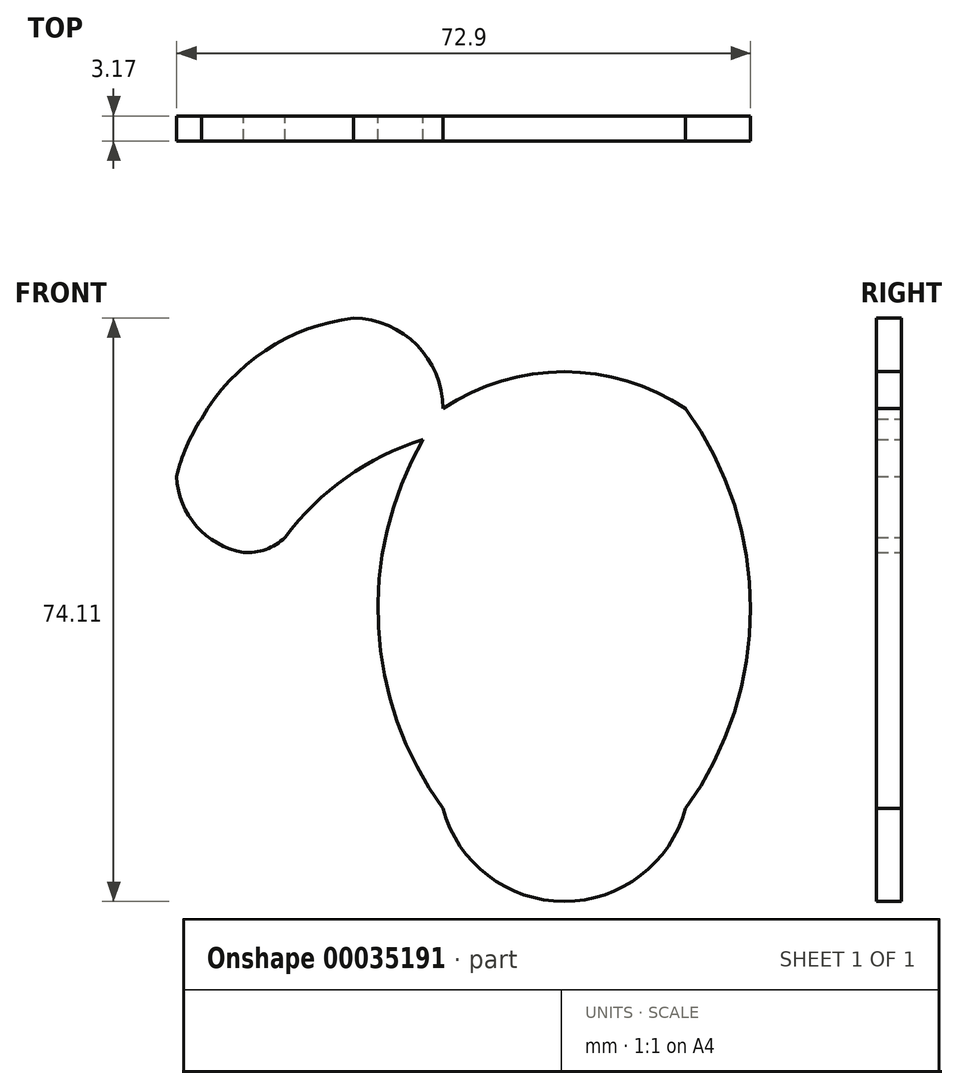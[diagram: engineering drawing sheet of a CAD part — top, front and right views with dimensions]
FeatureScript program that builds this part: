
annotation { "Feature Type Name" : "Feature", "Feature Type Description" : "" }
export const myFeature = defineFeature(function(context is Context, id is Id, definition is map)
    precondition{}
    {
        {
            var Q0;
            Q0=qCreatedBy(makeId("Front.planeOp"),FACE);
            var sketch = newSketch(context, id + "F0", { "sketchPlane" : qUnion([Q0])});
            skLineSegment(sketch, "E0.rect.bottom", {"start": v(15.4, -25.4) * mm, "end": v(-15.4, -25.4) * mm});
            skLineSegment(sketch, "E0.rect.top", {"start": v(15.4, 25.4) * mm, "end": v(-15.4, 25.4) * mm});
            skLineSegment(sketch, "E0.rect.left", {"start": v(15.4, -25.4) * mm, "end": v(15.4, 25.4) * mm});
            skLineSegment(sketch, "E0.rect.right", {"start": v(-15.4, -25.4) * mm, "end": v(-15.4, 25.4) * mm});
            skPoint(sketch, "E0.rect.middle", {"position": v(0, 0) * mm});
            skArc(sketch, "E1", {"start": v(-15.4, 25.4) * mm, "mid": v(-23.67, 0) * mm, "end": v(-15.4, -25.4) * mm});
            skLineSegment(sketch, "E2", {"start": v(0, 37.37) * mm, "end": v(0, -55.62) * mm, "construction": true});
            skArc(sketch, "E3", {"start": v(-15.4, -25.4) * mm, "mid": v(0, -37.2) * mm, "end": v(15.4, -25.4) * mm});
            skArc(sketch, "E4.MirrorCS", {"start": v(15.4, 25.4) * mm, "mid": v(23.67, 0) * mm, "end": v(15.4, -25.4) * mm});
            skArc(sketch, "E5", {"start": v(15.4, 25.4) * mm, "mid": v(0, 30.1) * mm, "end": v(-15.4, 25.4) * mm});
            skArc(sketch, "E6", {"start": v(-15.4, 25.4) * mm, "mid": v(-18.73, 33.5) * mm, "end": v(-26.8, 36.9) * mm});
            skArc(sketch, "E7", {"start": v(-26.8, 36.9) * mm, "mid": v(-37.96, 32.8) * mm, "end": v(-46.1, 24.12) * mm});
            skArc(sketch, "E8", {"start": v(-46.1, 24.12) * mm, "mid": v(-47.98, 20.6) * mm, "end": v(-49.23, 16.8) * mm});
            skArc(sketch, "E9", {"start": v(-49.23, 16.8) * mm, "mid": v(-46.7, 10.46) * mm, "end": v(-40.74, 7.15) * mm});
            skArc(sketch, "E10.MirrorCS", {"start": v(49.23, 16.8) * mm, "mid": v(46.7, 10.46) * mm, "end": v(40.74, 7.15) * mm});
            skArc(sketch, "E11.MirrorCS", {"start": v(46.1, 24.12) * mm, "mid": v(47.98, 20.6) * mm, "end": v(49.23, 16.8) * mm});
            skArc(sketch, "E12.MirrorCS", {"start": v(26.8, 36.9) * mm, "mid": v(37.96, 32.8) * mm, "end": v(46.1, 24.12) * mm});
            skArc(sketch, "E13.MirrorCS", {"start": v(15.4, 25.4) * mm, "mid": v(18.73, 33.5) * mm, "end": v(26.8, 36.9) * mm});
            skArc(sketch, "E14", {"start": v(-40.74, 7.15) * mm, "mid": v(-37.9, 7.53) * mm, "end": v(-35.47, 9.06) * mm});
            skArc(sketch, "E15", {"start": v(-17.94, 21.48) * mm, "mid": v(-27.68, 16.64) * mm, "end": v(-35.47, 9.06) * mm});
            skArc(sketch, "E16.MirrorCS", {"start": v(17.94, 21.48) * mm, "mid": v(27.68, 16.64) * mm, "end": v(35.47, 9.06) * mm});
            skArc(sketch, "E17.MirrorCS", {"start": v(40.74, 7.15) * mm, "mid": v(37.9, 7.53) * mm, "end": v(35.47, 9.06) * mm});
            skSolve(sketch);
        }
        {
            var Q0;
            {var subQ1=sQuery(id+"F0.wireOp",EDGE,"E6");Q0=makeQuery(id+"F0.imprint","IMPRINT",FACE,{"disambiguationData":[TD([[makeQuery(id+"F0.imprint","IMPRINT",EDGE,{"derivedFrom":subQ1}),1.0]])]});}
            var Q1;
            {var subQ2=sQuery(id+"F0.wireOp",EDGE,"E0.rect.right");Q1=makeQuery(id+"F0.imprint","IMPRINT",FACE,{"disambiguationData":[TD([[makeQuery(id+"F0.imprint","IMPRINT",EDGE,{"derivedFrom":subQ2}),1.0]])]});}
            var Q2;
            Q2=makeQuery(id+"F0.imprint","IMPRINT",FACE,{"disambiguationData":[TD([[makeQuery(id+"F0.imprint","IMPRINT",EDGE,{"derivedFrom":sQuery(id+"F0.wireOp",EDGE,"E0.rect.bottom")}),-1.0]])]});
            var Q3;
            Q3=makeQuery(id+"F0.imprint","IMPRINT",FACE,{"disambiguationData":[TD([[makeQuery(id+"F0.imprint","IMPRINT",EDGE,{"derivedFrom":sQuery(id+"F0.wireOp",EDGE,"E0.rect.top")}),-1.0]])]});
            var Q4;
            {var subQ2=sQuery(id+"F0.wireOp",EDGE,"E0.rect.left");Q4=makeQuery(id+"F0.imprint","IMPRINT",FACE,{"disambiguationData":[TD([[makeQuery(id+"F0.imprint","IMPRINT",EDGE,{"derivedFrom":subQ2}),-1.0]])]});}
            var Q5;
            Q5=makeQuery(id+"F0.imprint","IMPRINT",FACE,{"disambiguationData":[TD([[makeQuery(id+"F0.imprint","IMPRINT",EDGE,{"derivedFrom":sQuery(id+"F0.wireOp",EDGE,"E0.rect.bottom")}),1.0]])]});
            var Q6;
            Q6=makeQuery(id+"F0.imprint","IMPRINT",FACE,{"disambiguationData":[TD([[makeQuery(id+"F0.imprint","IMPRINT",EDGE,{"derivedFrom":sQuery(id+"F0.wireOp",EDGE,"E10.MirrorCS")}),-1.0]])]});
            extrude(context, id + "F1", {"entities" : qUnion([Q0, Q1, Q2, Q3, Q4, Q5, Q6]), "depth" : 3.17 * mm});
        }
    });
